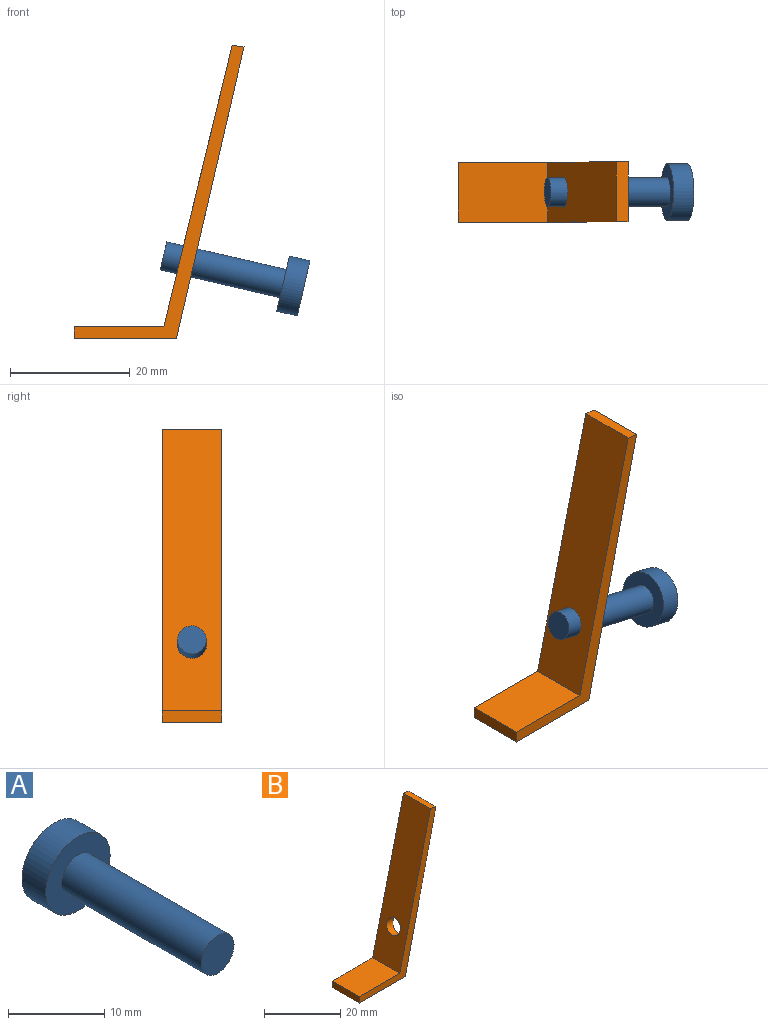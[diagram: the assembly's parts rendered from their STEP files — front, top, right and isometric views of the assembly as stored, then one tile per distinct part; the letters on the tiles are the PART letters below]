
ASSEMBLY  parts=2 mates=1
PART A: 5 faces, bbox 9.4x24x9.4 mm
  f0: cylinder r=2.4mm len=20.5mm, axis (0,1,0), area 309.1mm2, adj f1,f3
  f1: plane 4.8x4.8mm, normal (0,-1,0), area 18.1mm2, adj f0
  f2: cylinder r=4.72mm len=9.44mm, axis (0,1,0), area 103.8mm2, adj f3,f4
  f3: plane 9.44x9.44mm, normal (0,-1,0), area 51.8mm2, adj f0,f2
  f4: plane 9.44x9.44mm, normal (0,1,0), area 69.9mm2, adj f2
PART B: 9 faces, bbox 28.4x10x49 mm
  f0: plane 10x2mm, normal (-1,0,0), area 20mm2, adj f1,f5,f6,f7
  f1: plane 17.09x10mm, normal (0,0,-1), area 170.9mm2, adj f0,f2,f6,f7
  f2: plane 48.71x11.29mm, normal (0.97,0,-0.23), area 480.4mm2, adj f1,f3,f6,f7,f8
  f3: plane 10x1.98mm, normal (0.13,0,0.99), area 20mm2, adj f2,f4,f6,f7
  f4: plane 46.98x11.41mm, normal (-0.97,0,0.24), area 463.7mm2, adj f3,f5,f6,f7,f8
  f5: plane 15x10mm, normal (0,0,1), area 150mm2, adj f0,f4,f6,f7
  f6: plane 48.97x28.38mm, normal (0,-1,0), area 142.4mm2, adj f0,f1,f2,f3,f4,f5
  f7: plane 48.97x28.38mm, normal (0,1,0), area 142.4mm2, adj f0,f1,f2,f3,f4,f5
  f8: cylinder r=2.5mm len=5.41mm, axis (0.97,0,-0.23), area 37.3mm2, adj f2,f4
PLACE A rot(axis=(-0.11,0.11,-0.99),90.7deg) t=(-58.11,-79.57,49.81)mm
PLACE B t=(-70.61,-14.38,38.81)mm
MATE slider A.f0 <-> B.f8  axis (0.97,0,-0.23) through (-74.89,-19.38,38.33)mm
